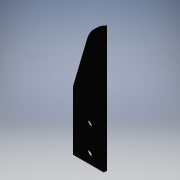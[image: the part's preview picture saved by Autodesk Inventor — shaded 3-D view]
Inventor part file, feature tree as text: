
AUTODESK INVENTOR PART (.ipt)
format: ipt  version: 2016 (Build 200138000, 138)  size: 124,928 bytes
history: native  units: in
note: dims shown in document units (in); Inventor stores cm internally (conversion verified against a paired STEP export)
features: extrude x2, sketch x2, reference x2
ambient origin geometry x8: Origin, YZ Plane, XZ Plane, XY Plane, X Axis, Y Axis, Z Axis, Center Point
bodies: Solid1 (feature_tree)
feature tree (6):
  extrude  "Extrusion1"  Depth=0.26in
  extrude  "Extrusion2"  Depth=1.0in
  sketch  "Sketch1"  dims[d1=0.26in d2=0.26in]
  reference  "Reference1"
  reference  "Reference2"
  sketch  "Sketch2"  dims[d3=1.0in d6=0.6in d7=0.6in d8=1.0in d9=0.125in d10=0.0in d11=1.0in d12=0.0in]
